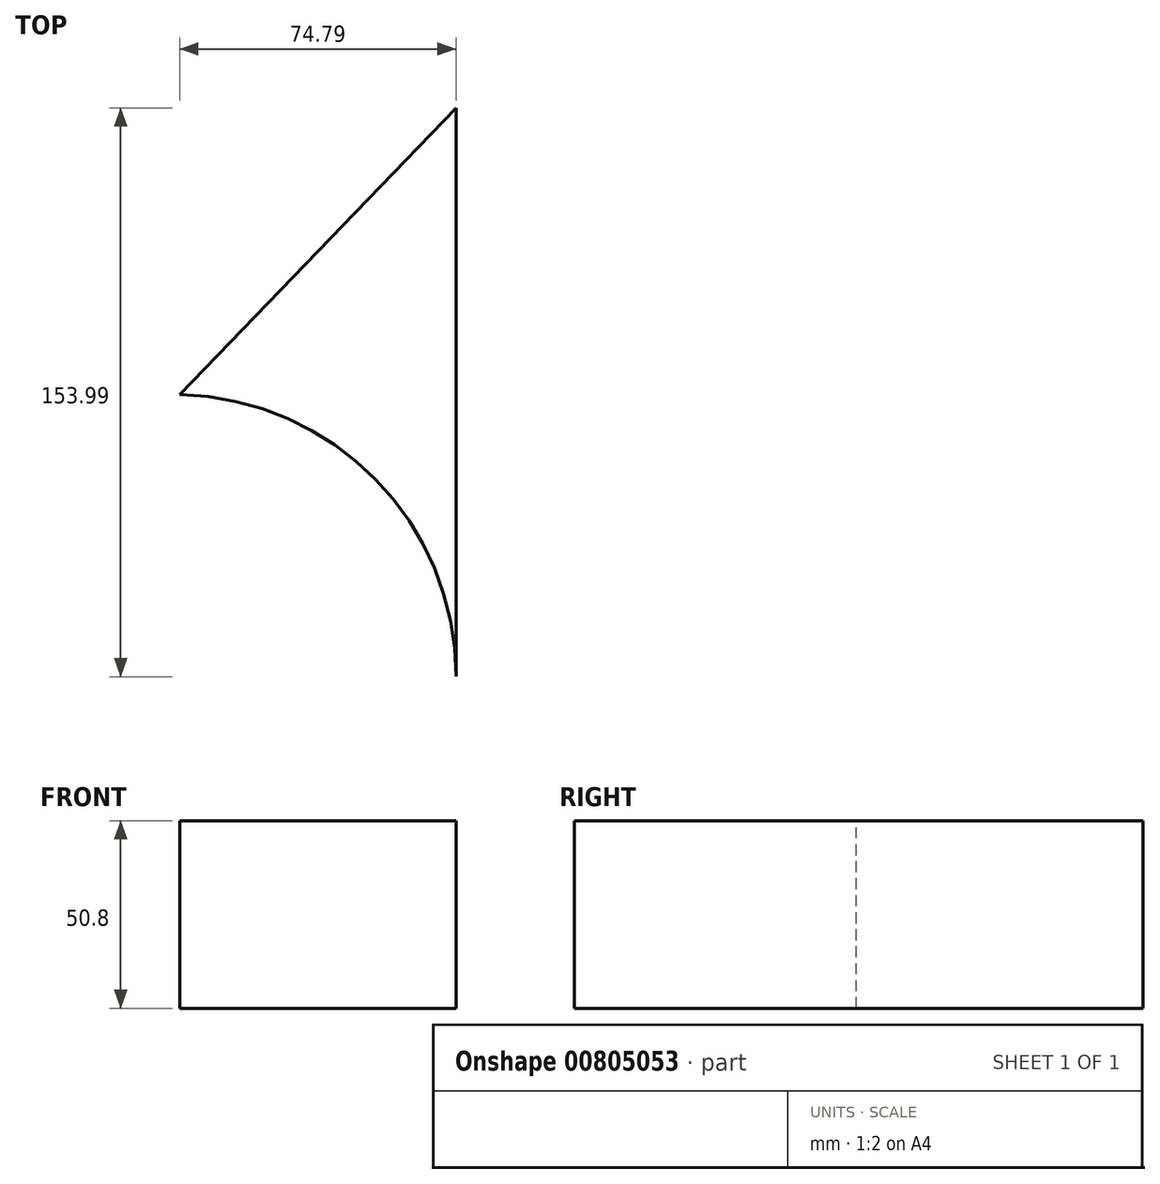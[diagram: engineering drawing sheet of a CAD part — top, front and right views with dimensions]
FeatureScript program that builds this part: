
annotation { "Feature Type Name" : "Feature", "Feature Type Description" : "" }
export const myFeature = defineFeature(function(context is Context, id is Id, definition is map)
    precondition{}
    {
        {
            var Q0;
            Q0=qCreatedBy(makeId("Top.planeOp"),FACE);
            var sketch = newSketch(context, id + "F0", { "sketchPlane" : qUnion([Q0])});
            skLineSegment(sketch, "E0", {"start": v(0, -76.37) * mm, "end": v(0, 77.62) * mm});
            skLineSegment(sketch, "E1", {"start": v(0, 77.62) * mm, "end": v(-74.79, 0) * mm});
            skArc(sketch, "E2", {"start": v(0, -76.37) * mm, "mid": v(-21.81, -22.92) * mm, "end": v(-74.79, 0) * mm});
            skSolve(sketch);
        }
        {
            var Q0;
            Q0 = qSketchRegion(id + "F0", true);
            extrude(context, id + "F1", {"entities" : qUnion([Q0]), "oppositeDirection" : true, "depth" : 25.4 * mm, "offsetDistance" : 25.4 * mm, "hasSecondDirection" : true, "secondDirectionOppositeDirection" : false, "secondDirectionDepth" : 25.4 * mm});
        }
    });
